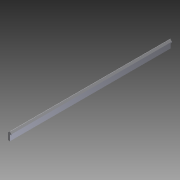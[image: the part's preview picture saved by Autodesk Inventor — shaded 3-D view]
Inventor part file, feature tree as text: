
AUTODESK INVENTOR PART (.ipt)
format: ipt  version: 2014 (Build 180170000, 170)  size: 94,720 bytes
history: native  units: in
note: dims shown in document units (in); Inventor stores cm internally (conversion verified against a paired STEP export)
features: fillet x1, other x1, imported_body x1
ambient origin geometry x8: Origin, YZ Plane, XZ Plane, XY Plane, X Axis, Y Axis, Z Axis, Center Point
bodies: Body1 (feature_tree)
feature tree (3):
  fillet  "Fillet1"  [1 undecoded]
  other  "BWC-T2-11"
  imported_body  "Base1"
note: 1 required parameter value undecoded (feature->parameter linkage not recoverable at this tier; creation-order binding heuristic only, values carry confidence <= 0.55)
